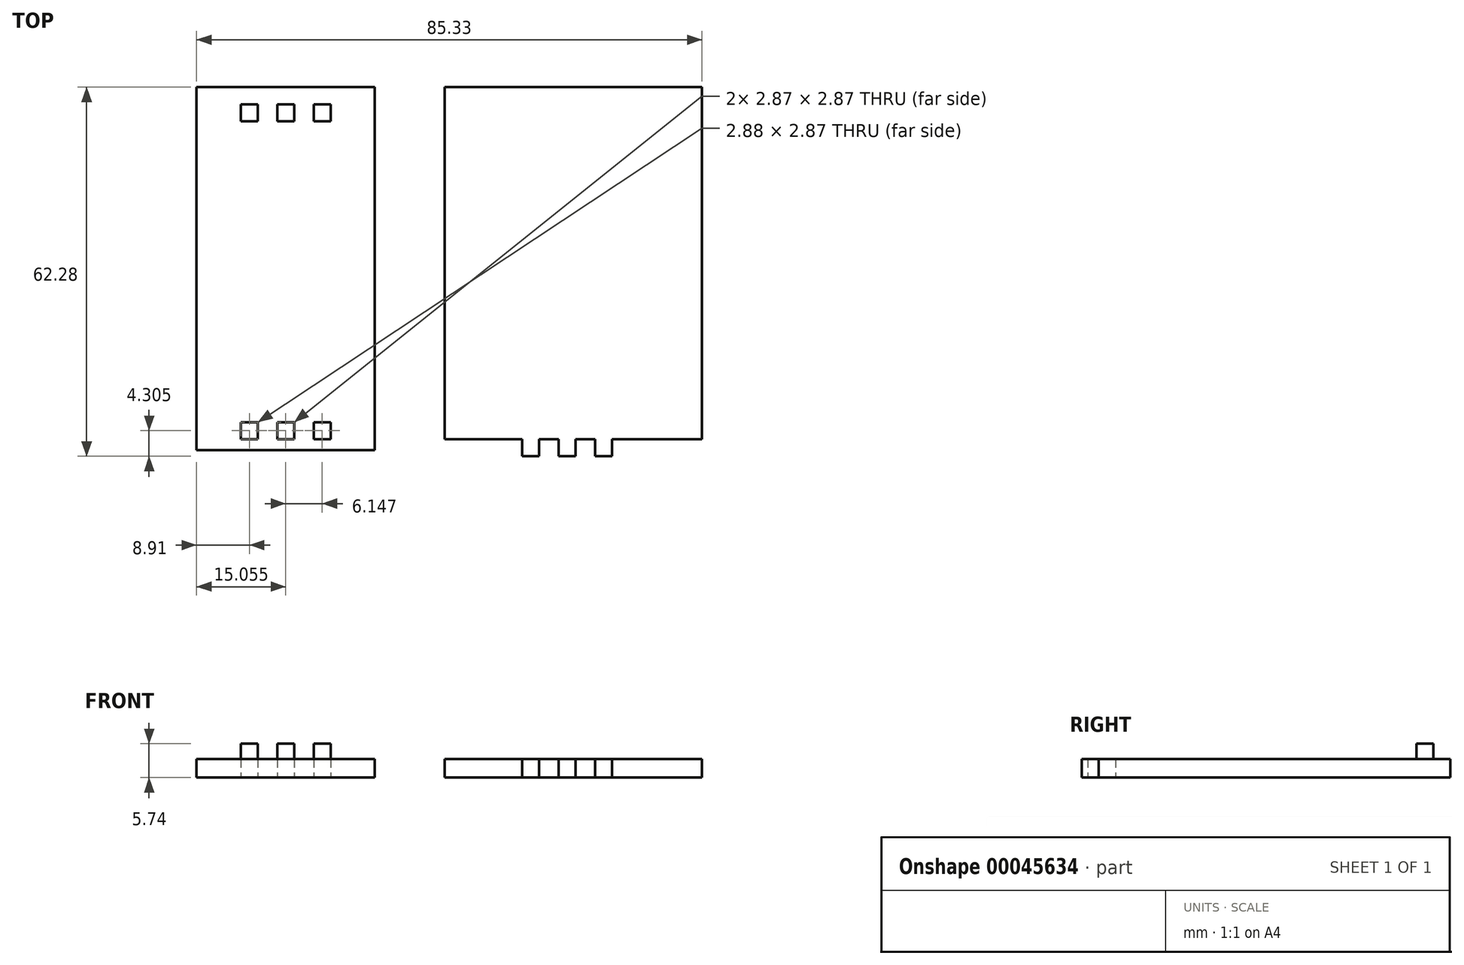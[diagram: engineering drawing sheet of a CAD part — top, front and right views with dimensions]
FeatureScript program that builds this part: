
annotation { "Feature Type Name" : "Feature", "Feature Type Description" : "" }
export const myFeature = defineFeature(function(context is Context, id is Id, definition is map)
    precondition{}
    {
        {
            var Q0;
            Q0=qCreatedBy(makeId("Top.planeOp"),FACE);
            var sketch = newSketch(context, id + "F0", { "sketchPlane" : qUnion([Q0])});
            skLineSegment(sketch, "E0.bottom", {"start": v(0, 0) * mm, "end": v(-2.87, 0) * mm});
            skLineSegment(sketch, "E0.top", {"start": v(0, 2.87) * mm, "end": v(-2.87, 2.87) * mm});
            skLineSegment(sketch, "E0.left", {"start": v(0, 0) * mm, "end": v(0, 2.87) * mm});
            skLineSegment(sketch, "E0.right", {"start": v(-2.87, 0) * mm, "end": v(-2.87, 2.87) * mm});
            skLineSegment(sketch, "E1.bottom", {"start": v(6.14, 0) * mm, "end": v(3.27, 0) * mm});
            skLineSegment(sketch, "E1.top", {"start": v(6.14, 2.87) * mm, "end": v(3.27, 2.87) * mm});
            skLineSegment(sketch, "E1.left", {"start": v(6.14, 0) * mm, "end": v(6.14, 2.87) * mm});
            skLineSegment(sketch, "E1.right", {"start": v(3.27, 0) * mm, "end": v(3.27, 2.87) * mm});
            skLineSegment(sketch, "E2.bottom", {"start": v(9.42, 2.87) * mm, "end": v(12.29, 2.87) * mm});
            skLineSegment(sketch, "E2.top", {"start": v(9.42, 0) * mm, "end": v(12.29, 0) * mm});
            skLineSegment(sketch, "E2.left", {"start": v(9.42, 2.87) * mm, "end": v(9.42, 0) * mm});
            skLineSegment(sketch, "E2.right", {"start": v(12.29, 2.87) * mm, "end": v(12.29, 0) * mm});
            skLineSegment(sketch, "E3.bottom", {"start": v(-10.35, 5.74) * mm, "end": v(19.74, 5.74) * mm});
            skLineSegment(sketch, "E3.top", {"start": v(-10.35, -55.5) * mm, "end": v(19.74, -55.5) * mm});
            skLineSegment(sketch, "E3.left", {"start": v(-10.35, 5.74) * mm, "end": v(-10.35, -55.5) * mm});
            skLineSegment(sketch, "E3.right", {"start": v(19.74, 5.74) * mm, "end": v(19.74, -55.5) * mm});
            skLineSegment(sketch, "E4", {"start": v(-2.88, -53.67) * mm, "end": v(0, -53.67) * mm});
            skLineSegment(sketch, "E5", {"start": v(-2.88, -50.8) * mm, "end": v(0, -50.8) * mm});
            skLineSegment(sketch, "E6.bottom", {"start": v(0, -53.67) * mm, "end": v(-2.88, -53.67) * mm});
            skLineSegment(sketch, "E6.top", {"start": v(0, -50.8) * mm, "end": v(-2.88, -50.8) * mm});
            skLineSegment(sketch, "E6.left", {"start": v(0, -53.67) * mm, "end": v(0, -50.8) * mm});
            skLineSegment(sketch, "E6.right", {"start": v(-2.88, -53.67) * mm, "end": v(-2.88, -50.8) * mm});
            skLineSegment(sketch, "E7", {"start": v(3.27, -50.8) * mm, "end": v(3.27, -53.67) * mm});
            skLineSegment(sketch, "E8", {"start": v(3.27, -53.67) * mm, "end": v(6.14, -53.67) * mm});
            skLineSegment(sketch, "E9", {"start": v(6.14, -53.67) * mm, "end": v(6.14, -50.8) * mm});
            skLineSegment(sketch, "E10", {"start": v(3.27, -50.8) * mm, "end": v(6.14, -50.8) * mm});
            skLineSegment(sketch, "E11", {"start": v(12.29, -50.8) * mm, "end": v(12.29, -53.67) * mm});
            skLineSegment(sketch, "E12", {"start": v(12.29, -53.67) * mm, "end": v(9.42, -53.67) * mm});
            skLineSegment(sketch, "E13", {"start": v(9.42, -53.67) * mm, "end": v(9.42, -50.8) * mm});
            skPoint(sketch, "E13.endSnap0", {"position": v(6.14, -50.8) * mm});
            skLineSegment(sketch, "E14", {"start": v(9.42, -50.8) * mm, "end": v(9.42, -53.67) * mm});
            skLineSegment(sketch, "E15.right", {"start": v(0, -50.8) * mm, "end": v(0, -53.67) * mm});
            skLineSegment(sketch, "E16.right", {"start": v(6.14, -50.8) * mm, "end": v(6.14, -53.67) * mm});
            skLineSegment(sketch, "E17.bottom", {"start": v(9.42, -50.8) * mm, "end": v(12.29, -50.8) * mm});
            skLineSegment(sketch, "E17.top", {"start": v(9.42, -53.67) * mm, "end": v(12.29, -53.67) * mm});
            skLineSegment(sketch, "E18.left", {"start": v(-2.88, -50.8) * mm, "end": v(-2.88, -53.67) * mm});
            skLineSegment(sketch, "E19", {"start": v(31.54, -53.67) * mm, "end": v(31.54, 5.74) * mm});
            skLineSegment(sketch, "E20", {"start": v(31.54, 5.74) * mm, "end": v(74.98, 5.74) * mm});
            skLineSegment(sketch, "E21", {"start": v(74.98, 5.74) * mm, "end": v(74.98, -53.67) * mm});
            skLineSegment(sketch, "E22", {"start": v(74.98, -53.67) * mm, "end": v(59.78, -53.67) * mm});
            skLineSegment(sketch, "E23.top", {"start": v(44.62, -56.54) * mm, "end": v(47.49, -56.54) * mm});
            skLineSegment(sketch, "E23.left", {"start": v(44.62, -53.67) * mm, "end": v(44.62, -56.54) * mm});
            skLineSegment(sketch, "E23.right", {"start": v(47.49, -53.67) * mm, "end": v(47.49, -56.54) * mm});
            skLineSegment(sketch, "E24.top", {"start": v(50.76, -56.54) * mm, "end": v(53.63, -56.54) * mm});
            skLineSegment(sketch, "E24.left", {"start": v(50.76, -53.67) * mm, "end": v(50.76, -56.54) * mm});
            skLineSegment(sketch, "E24.right", {"start": v(53.63, -53.67) * mm, "end": v(53.63, -56.54) * mm});
            skLineSegment(sketch, "E25.top", {"start": v(56.9, -56.54) * mm, "end": v(59.78, -56.54) * mm});
            skLineSegment(sketch, "E25.left", {"start": v(56.9, -53.67) * mm, "end": v(56.9, -56.54) * mm});
            skLineSegment(sketch, "E25.right", {"start": v(59.78, -53.67) * mm, "end": v(59.78, -56.54) * mm});
            skLineSegment(sketch, "E26.trimOffspring", {"start": v(50.76, -53.67) * mm, "end": v(47.49, -53.67) * mm});
            skLineSegment(sketch, "E27.trimOffspring", {"start": v(56.9, -53.67) * mm, "end": v(53.63, -53.67) * mm});
            skLineSegment(sketch, "E28.trimOffspring", {"start": v(44.62, -53.67) * mm, "end": v(31.54, -53.67) * mm});
            skSolve(sketch);
        }
        {
            var Q0;
            Q0 = qSketchRegion(id + "F0", true);
            extrude(context, id + "F1", {"entities" : qUnion([Q0]), "depth" : 3.15 * mm});
        }
        {
            var Q0;
            Q0=makeQuery(id+"F0.imprint","IMPRINT",FACE,{"disambiguationData":[TD([[makeQuery(id+"F0.imprint","IMPRINT",EDGE,{"derivedFrom":sQuery(id+"F0.wireOp",EDGE,"E2.bottom")}),-1.0]])]});
            var Q1;
            Q1=makeQuery(id+"F0.imprint","IMPRINT",FACE,{"disambiguationData":[TD([[makeQuery(id+"F0.imprint","IMPRINT",EDGE,{"derivedFrom":sQuery(id+"F0.wireOp",EDGE,"E1.bottom")}),-1.0]])]});
            var Q2;
            Q2=makeQuery(id+"F0.imprint","IMPRINT",FACE,{"disambiguationData":[TD([[makeQuery(id+"F0.imprint","IMPRINT",EDGE,{"derivedFrom":sQuery(id+"F0.wireOp",EDGE,"E0.bottom")}),-1.0]])]});
            extrude(context, id + "F2", {"entities" : qUnion([Q0, Q1, Q2]), "operationType" : NewBodyOperationType.ADD, "depth" : 5.74 * mm});
        }
    });
